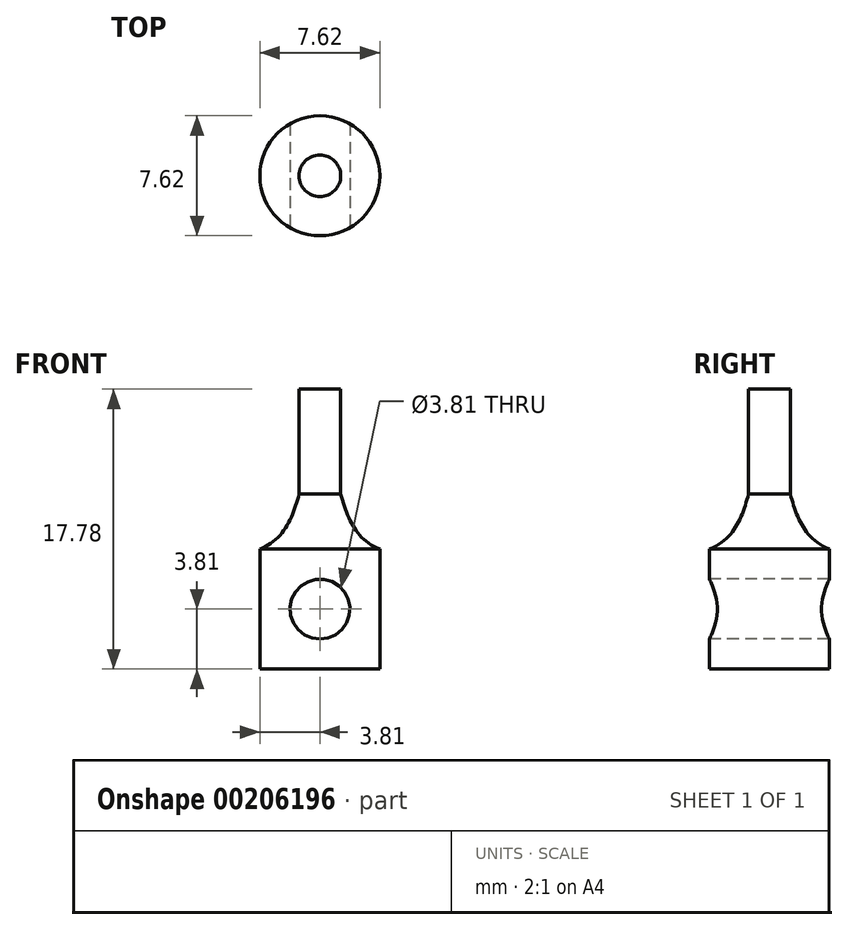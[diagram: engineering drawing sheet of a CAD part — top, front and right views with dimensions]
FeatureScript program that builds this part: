
annotation { "Feature Type Name" : "Feature", "Feature Type Description" : "" }
export const myFeature = defineFeature(function(context is Context, id is Id, definition is map)
    precondition{}
    {
        {
            var Q0;
            Q0=qCreatedBy(makeId("Top.planeOp"),FACE);
            var sketch = newSketch(context, id + "F0", { "sketchPlane" : qUnion([Q0])});
            skCircle(sketch, "E0", {"center": v(0, 0) * mm, "radius": 1.32 * mm});
            skCircle(sketch, "E1", {"center": v(0, 0) * mm, "radius": 3.81 * mm});
            skSolve(sketch);
        }
        {
            var Q0;
            Q0 = qSketchRegion(id + "F0", true);
            var Q1;
            Q1=makeQuery(id+"F0.imprint","IMPRINT",FACE,{"disambiguationData":[TD([[makeQuery(id+"F0.imprint","IMPRINT",EDGE,{"derivedFrom":sQuery(id+"F0.wireOp",EDGE,"E0")}),1.0]])]});
            extrude(context, id + "F1", {"entities" : qUnion([Q0, Q1]), "depth" : 7.62 * mm});
        }
        {
            var Q0;
            Q0=makeQuery(id+"F0.imprint","IMPRINT",FACE,{"disambiguationData":[TD([[makeQuery(id+"F0.imprint","IMPRINT",EDGE,{"derivedFrom":sQuery(id+"F0.wireOp",EDGE,"E0")}),1.0]])]});
            extrude(context, id + "F2", {"entities" : qUnion([Q0]), "operationType" : NewBodyOperationType.ADD, "depth" : 17.78 * mm});
        }
        {
            var Q0;
            Q0=qCreatedBy(makeId("Front.planeOp"),FACE);
            var sketch = newSketch(context, id + "F3", { "sketchPlane" : qUnion([Q0])});
            skCircle(sketch, "E2", {"center": v(0, 3.81) * mm, "radius": 1.9 * mm});
            skLineSegment(sketch, "E3.0", {"start": v(-3.81, 7.62) * mm, "end": v(3.81, 7.62) * mm});
            skLineSegment(sketch, "E4", {"start": v(0, 0) * mm, "end": v(0, 7.62) * mm, "construction": true});
            skSolve(sketch);
        }
        {
            var Q0;
            Q0 = qSketchRegion(id + "F3", true);
            extrude(context, id + "F4", {"entities" : qUnion([Q0]), "operationType" : NewBodyOperationType.REMOVE, "oppositeDirection" : true, "depth" : 25.4 * mm, "hasSecondDirection" : true, "secondDirectionOppositeDirection" : false, "secondDirectionDepth" : 25.4 * mm});
        }
        {
            var Q0;
            Q0=qCreatedBy(makeId("Front.planeOp"),FACE);
            var sketch = newSketch(context, id + "F5", { "sketchPlane" : qUnion([Q0])});
            skLineSegment(sketch, "E5.0", {"start": v(-3.81, 7.62) * mm, "end": v(3.81, 7.62) * mm});
            skFitSpline(sketch, "E6", {"points": [v(3.81, 7.62) * mm, v(0, 15.04) * mm], "startDerivative": vector(-8.39, 3.43) * mm, "endDerivative": vector(-4.74, 8.63) * mm});
            skLineSegment(sketch, "E7", {"start": v(0, 15.04) * mm, "end": v(0, 7.62) * mm});
            skSolve(sketch);
        }
        {
            var Q0;
            Q0 = qSketchRegion(id + "F5", true);
            var Q1;
            Q1=makeQuery(id+"F2.opExtrude","CAP_EDGE",EDGE,{"disambiguationData":[OSD([sQuery(id+"F0.wireOp",EDGE,"E0")])],"isStart":false});
            revolve(context, id + "F6", {"operationType" : NewBodyOperationType.ADD, "entities" : qUnion([Q0]), "axis" : qUnion([Q1]), "revolveType" : RevolveType.FULL});
        }
    });
